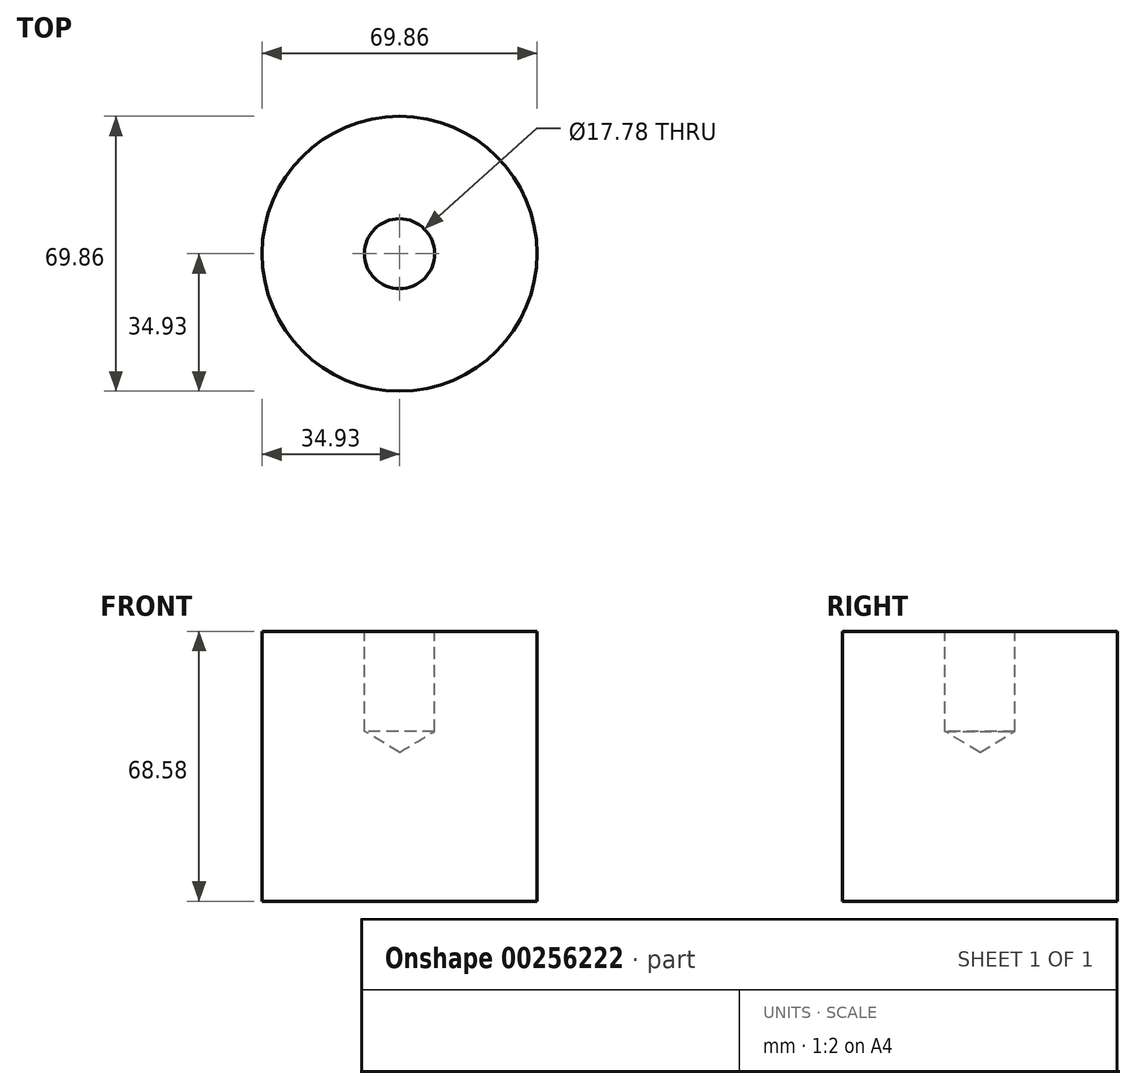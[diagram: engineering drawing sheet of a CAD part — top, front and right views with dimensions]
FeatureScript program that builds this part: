
annotation { "Feature Type Name" : "Feature", "Feature Type Description" : "" }
export const myFeature = defineFeature(function(context is Context, id is Id, definition is map)
    precondition{}
    {
        {
            var Q0;
            Q0=qCreatedBy(makeId("Top.planeOp"),FACE);
            var sketch = newSketch(context, id + "F0", { "sketchPlane" : qUnion([Q0])});
            skCircle(sketch, "E0", {"center": v(0, 0) * mm, "radius": 34.93 * mm});
            skSolve(sketch);
        }
        {
            var Q0;
            Q0=makeQuery(id+"F0.imprint","IMPRINT",FACE,{"disambiguationData":[TD([[makeQuery(id+"F0.imprint","IMPRINT",EDGE,{"derivedFrom":sQuery(id+"F0.wireOp",EDGE,"E0")}),1.0]])]});
            extrude(context, id + "F1", {"entities" : qUnion([Q0]), "oppositeDirection" : true, "depth" : 68.58 * mm});
        }
        {
            var Q0;
            Q0=qCreatedBy(makeId("Top.planeOp"),FACE);
            var sketch = newSketch(context, id + "F2", { "sketchPlane" : qUnion([Q0])});
            skCircle(sketch, "E1", {"center": v(0, 0) * mm, "radius": 8.9 * mm});
            skSolve(sketch);
        }
        {
            var Q0;
            Q0=sQuery(id+"F2.wireOp",VERTEX,"E1.center");
            var Q1;
            Q1=makeQuery(id+"F1.opExtrude","SWEPT_BODY",BODY,{"disambiguationData":[OSD([sQuery(id+"F0.wireOp",EDGE,"E0")])]});
            hole(context, id + "F3", {"style" : HoleStyle.SIMPLE, "endStyle" : HoleEndStyle.BLIND, "holeDiameter" : 17.78 * mm, "holeDepth" : 25.4 * mm, "tappedDepth" : 12.7 * mm, "tapClearance" : 3, "startFromSketch" : true, "locations" : qUnion([Q0]), "scope" : qUnion([Q1])});
        }
    });
